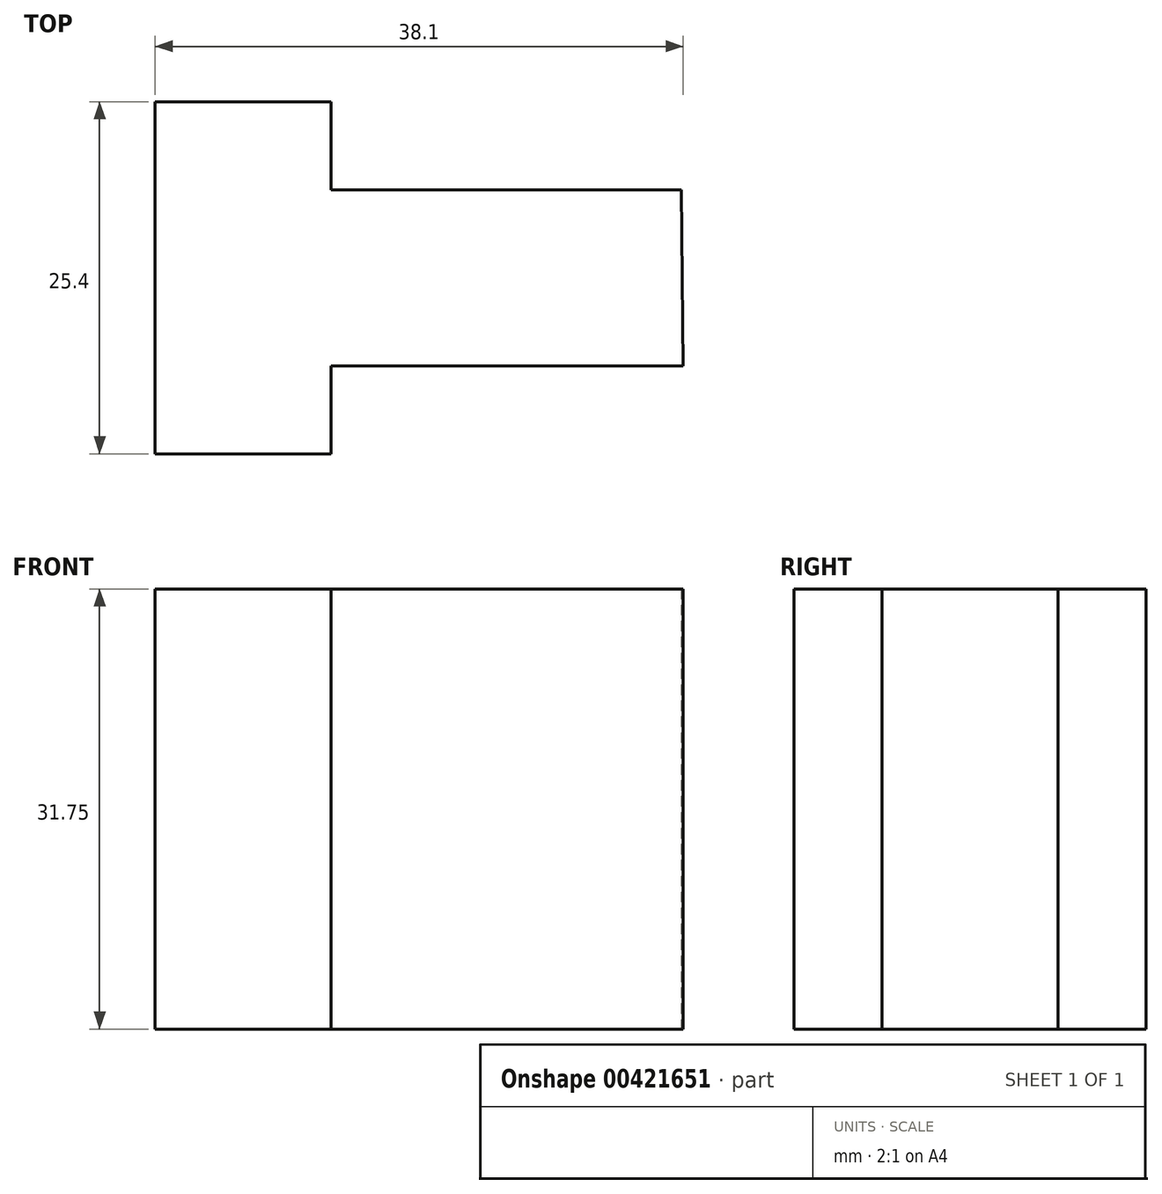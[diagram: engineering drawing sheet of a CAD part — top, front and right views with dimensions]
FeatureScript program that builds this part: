
annotation { "Feature Type Name" : "Feature", "Feature Type Description" : "" }
export const myFeature = defineFeature(function(context is Context, id is Id, definition is map)
    precondition{}
    {
        {
            var Q0;
            Q0=qCreatedBy(makeId("Top.planeOp"),FACE);
            var sketch = newSketch(context, id + "F0", { "sketchPlane" : qUnion([Q0])});
            skLineSegment(sketch, "E0", {"start": v(0, 0) * mm, "end": v(0, 25.4) * mm});
            skLineSegment(sketch, "E1", {"start": v(0, 25.4) * mm, "end": v(12.7, 25.4) * mm});
            skLineSegment(sketch, "E2", {"start": v(12.7, 25.4) * mm, "end": v(12.7, 19.05) * mm});
            skLineSegment(sketch, "E3", {"start": v(12.7, 19.05) * mm, "end": v(37.96, 19.05) * mm});
            skLineSegment(sketch, "E4", {"start": v(0, 0) * mm, "end": v(12.7, 0) * mm});
            skLineSegment(sketch, "E5", {"start": v(12.7, 0) * mm, "end": v(12.7, 6.35) * mm});
            skLineSegment(sketch, "E6", {"start": v(12.7, 6.35) * mm, "end": v(38.1, 6.35) * mm});
            skLineSegment(sketch, "E7", {"start": v(38.1, 6.35) * mm, "end": v(37.96, 19.05) * mm});
            skSolve(sketch);
        }
        {
            var Q0;
            Q0 = qSketchRegion(id + "F0", true);
            extrude(context, id + "F1", {"entities" : qUnion([Q0]), "depth" : 31.75 * mm});
        }
    });
